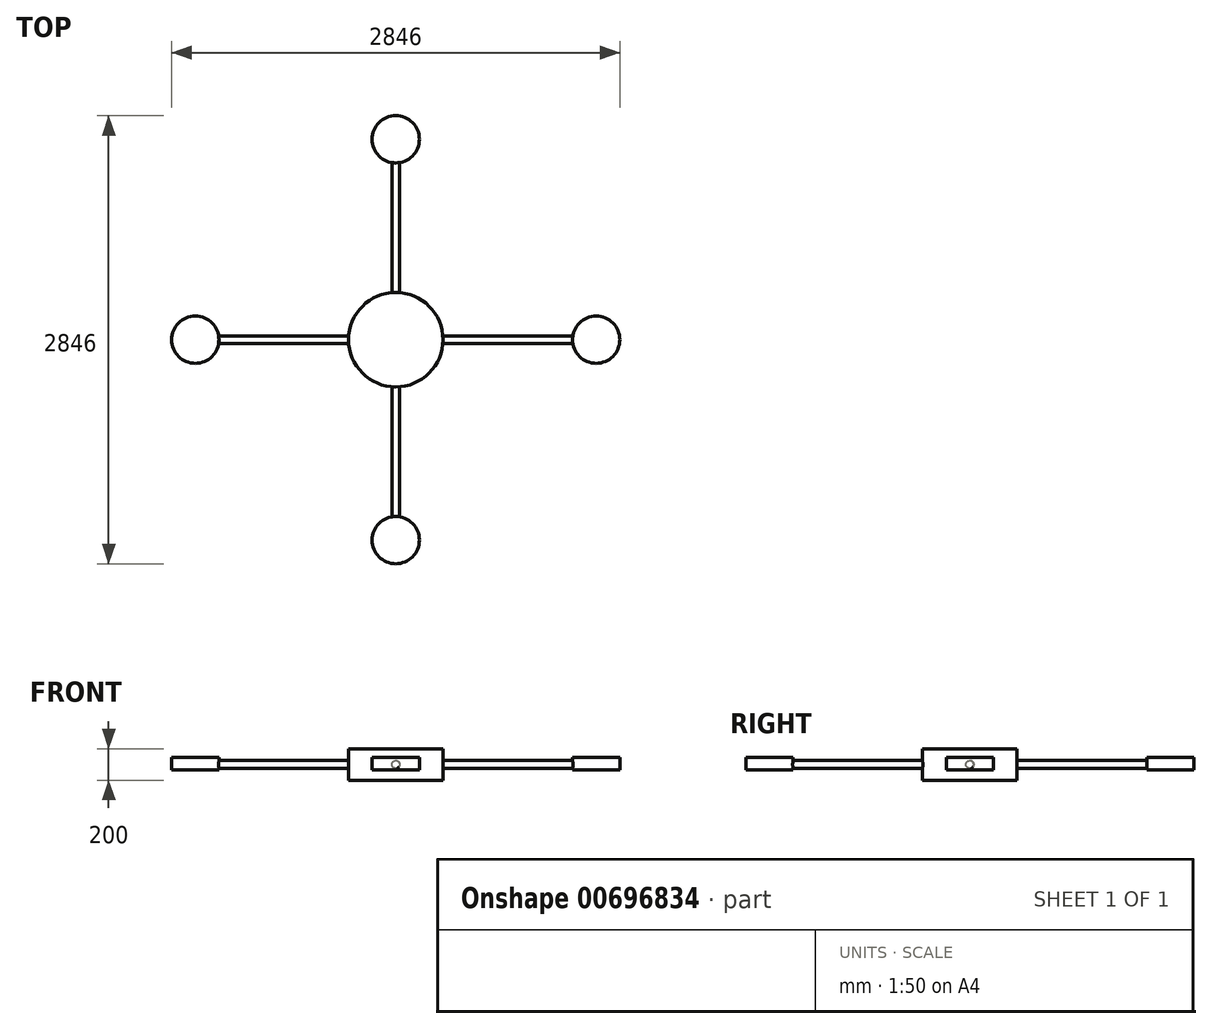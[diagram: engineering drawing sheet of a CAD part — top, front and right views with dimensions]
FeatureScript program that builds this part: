
annotation { "Feature Type Name" : "Feature", "Feature Type Description" : "" }
export const myFeature = defineFeature(function(context is Context, id is Id, definition is map)
    precondition{}
    {
        {
            var Q0;
            Q0=qCreatedBy(makeId("Top.planeOp"),FACE);
            var sketch = newSketch(context, id + "F0", { "sketchPlane" : qUnion([Q0])});
            skCircle(sketch, "E0", {"center": v(0, 0) * mm, "radius": 300 * mm});
            skSolve(sketch);
        }
        {
            var Q0;
            Q0=makeQuery(id+"F0.imprint","IMPRINT",FACE,{"disambiguationData":[TD([[makeQuery(id+"F0.imprint","IMPRINT",EDGE,{"derivedFrom":sQuery(id+"F0.wireOp",EDGE,"E0")}),1.0]])]});
            extrude(context, id + "F1", {"entities" : qUnion([Q0]), "depth" : 200 * mm, "offsetDistance" : 25 * mm});
        }
        {
            var Q0;
            Q0=qCreatedBy(makeId("Front.planeOp"),FACE);
            var sketch = newSketch(context, id + "F2", { "sketchPlane" : qUnion([Q0])});
            skCircle(sketch, "E1", {"center": v(0, 100) * mm, "radius": 25 * mm});
            skSolve(sketch);
        }
        {
            var Q0;
            Q0 = qSketchRegion(id + "F2", true);
            extrude(context, id + "F3", {"entities" : qUnion([Q0]), "operationType" : NewBodyOperationType.ADD, "depth" : 1273 * mm, "offsetDistance" : 25 * mm, "hasSecondDirection" : true, "secondDirectionOppositeDirection" : true, "secondDirectionDepth" : 1273 * mm});
        }
        {
            var Q0;
            Q0=makeQuery(id+"F1.opExtrude","SWEPT_BODY",BODY,{"disambiguationData":[OSD([sQuery(id+"F0.wireOp",EDGE,"E0")])]});
            var Q1;
            Q1=makeQuery(id+"F1.opExtrude","CAP_EDGE",EDGE,{"disambiguationData":[OSD([sQuery(id+"F0.wireOp",EDGE,"E0")])],"isStart":false});
            circularPattern(context, id + "F4", {"operationType" : NewBodyOperationType.ADD, "entities" : qUnion([Q0]), "axis" : qUnion([Q1]), "angle" : 90 * degree, "instanceCount" : 2, "equalSpace" : true});
        }
        {
            var Q0;
            Q0=makeQuery(id+"F3.opExtrude","CAP_FACE",FACE,{"disambiguationData":[OSD([sQuery(id+"F2.wireOp",EDGE,"E1")])],"isStart":false});
            var sketch = newSketch(context, id + "F5", { "sketchPlane" : qUnion([Q0])});
            skLineSegment(sketch, "E2.bottom", {"start": v(10.13, 106.05) * mm, "end": v(-10.13, 106.05) * mm});
            skLineSegment(sketch, "E2.top", {"start": v(10.13, 93.95) * mm, "end": v(-10.13, 93.95) * mm});
            skLineSegment(sketch, "E2.left", {"start": v(10.13, 106.05) * mm, "end": v(10.13, 93.95) * mm});
            skLineSegment(sketch, "E2.right", {"start": v(-10.13, 106.05) * mm, "end": v(-10.13, 93.95) * mm});
            skPoint(sketch, "E2.middle", {"position": v(0, 100) * mm});
            skSolve(sketch);
        }
        {
            var Q0;
            Q0=makeQuery(id+"F5.imprint","IMPRINT",FACE,{"disambiguationData":[TD([[makeQuery(id+"F5.imprint","IMPRINT",EDGE,{"derivedFrom":sQuery(id+"F5.wireOp",EDGE,"E2.bottom")}),1.0]])]});
            extrude(context, id + "F6", {"entities" : qUnion([Q0]), "operationType" : NewBodyOperationType.ADD, "depth" : 25 * mm, "offsetDistance" : 25 * mm});
        }
        {
            var Q0;
            Q0=makeQuery(id+"F6.opExtrude","SWEPT_FACE",FACE,{"disambiguationData":[OSD([sQuery(id+"F5.wireOp",EDGE,"E2.bottom")])]});
            var sketch = newSketch(context, id + "F7", { "sketchPlane" : qUnion([Q0])});
            skCircle(sketch, "E3", {"center": v(0, -1273) * mm, "radius": 150 * mm});
            skSolve(sketch);
        }
        {
            var Q0;
            Q0=makeQuery(id+"F7.imprint","IMPRINT",FACE,{"disambiguationData":[TD([[makeQuery(id+"F7.imprint","IMPRINT",EDGE,{"derivedFrom":sQuery(id+"F7.wireOp",EDGE,"E3")}),1.0]])]});
            var Q1;
            {var subQ0=sQuery(id+"F5.wireOp",EDGE,"E2.bottom");Q1=makeQuery(id+"F7.imprint","IMPRINT",FACE,{"disambiguationData":[TD([[makeQuery(id+"F7.imprint","IMPRINT",EDGE,{"derivedFrom":makeQuery(id+"F6.opExtrude","CAP_EDGE",EDGE,{"disambiguationData":[OSD([subQ0])],"isStart":false})}),-1.0]])]});}
            extrude(context, id + "F8", {"entities" : qUnion([Q0, Q1]), "operationType" : NewBodyOperationType.ADD, "oppositeDirection" : true, "depth" : 40 * mm, "offsetDistance" : 25 * mm, "hasSecondDirection" : true, "secondDirectionOppositeDirection" : false, "secondDirectionDepth" : 40 * mm});
        }
        {
            var Q0;
            Q0=makeQuery(id+"F1.opExtrude","SWEPT_BODY",BODY,{"disambiguationData":[OSD([sQuery(id+"F0.wireOp",EDGE,"E0")])]});
            var Q1;
            Q1=makeQuery(id+"F1.opExtrude","CAP_EDGE",EDGE,{"disambiguationData":[OSD([sQuery(id+"F0.wireOp",EDGE,"E0")])],"isStart":false});
            circularPattern(context, id + "F9", {"operationType" : NewBodyOperationType.ADD, "entities" : qUnion([Q0]), "axis" : qUnion([Q1]), "angle" : 360 * degree, "instanceCount" : 4, "equalSpace" : true});
        }
    });
